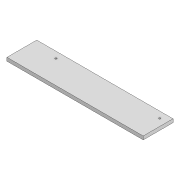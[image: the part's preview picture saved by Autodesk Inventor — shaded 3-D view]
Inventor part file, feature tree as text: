
AUTODESK INVENTOR PART (.ipt)
format: ipt  version: 2022 (Build 260153000, 153)  size: 87,552 bytes
history: native  units: mm
features: extrude x1, sketch x1
ambient origin geometry x8: Origin, YZ Plane, XZ Plane, XY Plane, X Axis, Y Axis, Z Axis, Center Point
bodies: Solid1 (feature_tree)
feature tree (2):
  extrude  "Extrusion1"  Depth=70.0mm
  sketch  "Sketch1"  dims[d0=320.0mm d1=70.0mm d2=4.0mm d3=4.0mm d4=243.651mm d5=60.0mm d6=15.0mm d7=15.0mm d8=8.0mm d9=0.0mm]
